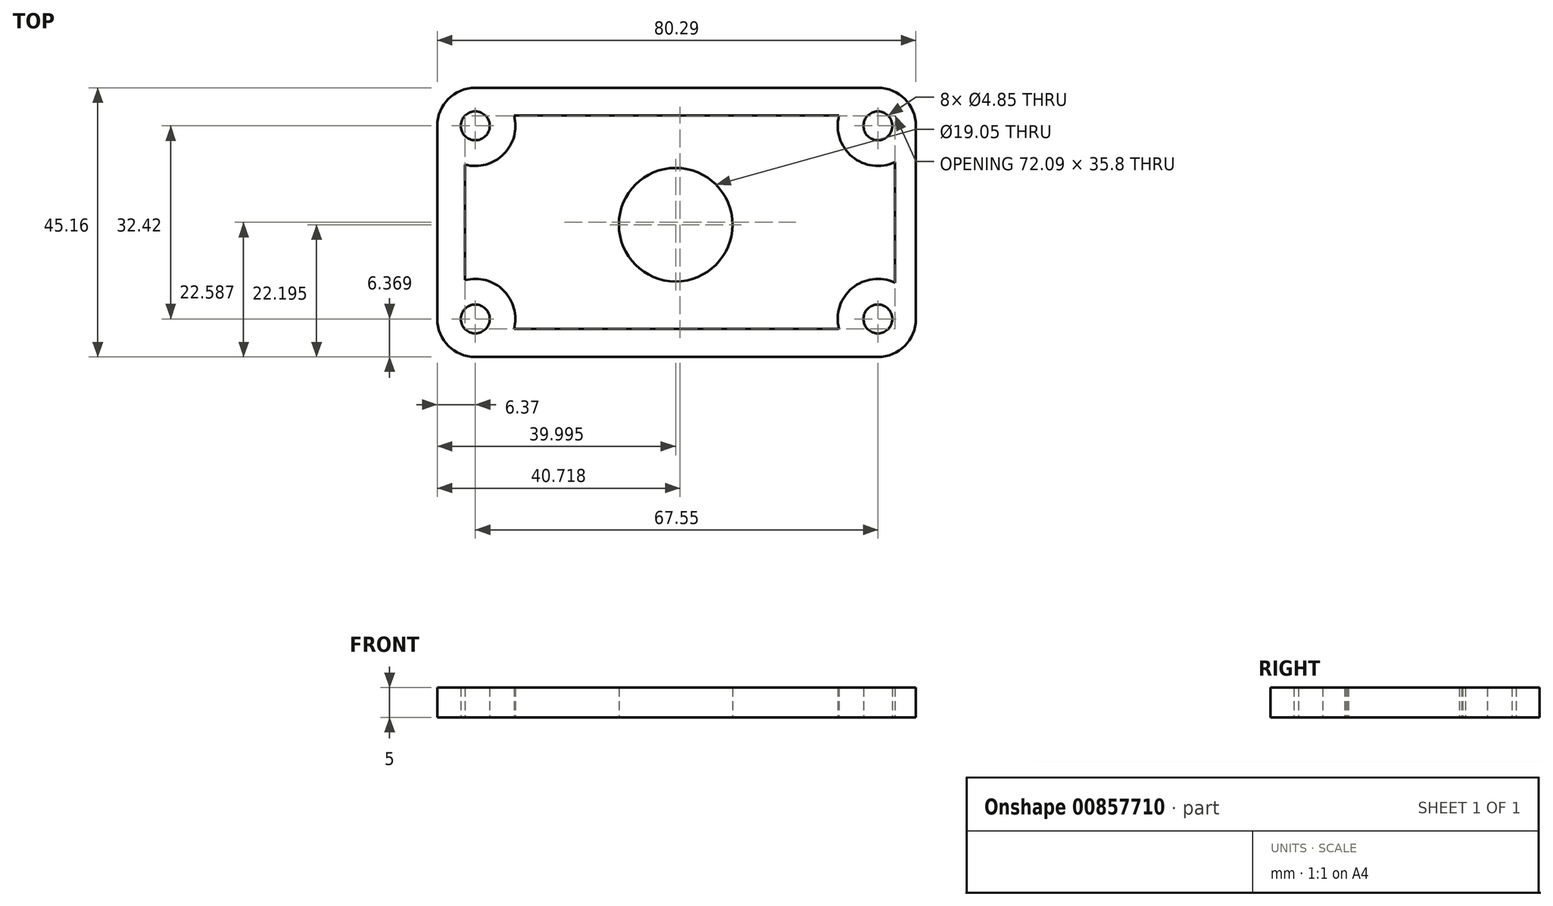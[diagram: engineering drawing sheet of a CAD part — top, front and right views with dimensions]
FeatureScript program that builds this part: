
annotation { "Feature Type Name" : "Feature", "Feature Type Description" : "" }
export const myFeature = defineFeature(function(context is Context, id is Id, definition is map)
    precondition{}
    {
        {
            var Q0;
            Q0=qCreatedBy(makeId("Top.planeOp"),FACE);
            var sketch = newSketch(context, id + "F0", { "sketchPlane" : qUnion([Q0])});
            skLineSegment(sketch, "E0.bottom", {"start": v(-49.8, 48.64) * mm, "end": v(17.74, 48.64) * mm});
            skLineSegment(sketch, "E0.top", {"start": v(-49.8, 3.48) * mm, "end": v(17.74, 3.48) * mm});
            skLineSegment(sketch, "E0.left", {"start": v(-56.18, 42.27) * mm, "end": v(-56.18, 9.85) * mm});
            skLineSegment(sketch, "E0.right", {"start": v(24.11, 42.27) * mm, "end": v(24.11, 9.85) * mm});
            skArc(sketch, "E1.filletArc", {"start": v(-49.8, 48.64) * mm, "mid": v(-54.32, 46.78) * mm, "end": v(-56.18, 42.27) * mm});
            skArc(sketch, "E2.filletArc", {"start": v(-56.18, 9.85) * mm, "mid": v(-54.32, 5.34) * mm, "end": v(-49.8, 3.48) * mm});
            skArc(sketch, "E3.filletArc", {"start": v(17.74, 3.48) * mm, "mid": v(22.25, 5.34) * mm, "end": v(24.11, 9.85) * mm});
            skArc(sketch, "E4.filletArc", {"start": v(24.11, 42.27) * mm, "mid": v(22.25, 46.78) * mm, "end": v(17.74, 48.64) * mm});
            skCircle(sketch, "E5", {"center": v(-49.8, 42.27) * mm, "radius": 2.42 * mm});
            skCircle(sketch, "E6", {"center": v(-49.8, 9.85) * mm, "radius": 2.42 * mm});
            skCircle(sketch, "E7", {"center": v(17.74, 9.85) * mm, "radius": 2.42 * mm});
            skCircle(sketch, "E8", {"center": v(17.74, 42.27) * mm, "radius": 2.42 * mm});
            skLineSegment(sketch, "E9", {"start": v(20.58, 36.16) * mm, "end": v(20.58, 16.17) * mm});
            skLineSegment(sketch, "E10", {"start": v(-43.29, 8.16) * mm, "end": v(11.22, 8.16) * mm});
            skLineSegment(sketch, "E11", {"start": v(-43.3, 43.97) * mm, "end": v(11.22, 43.97) * mm});
            skLineSegment(sketch, "E12", {"start": v(-51.5, 35.75) * mm, "end": v(-51.5, 16.17) * mm});
            skArc(sketch, "E13", {"start": v(-51.5, 35.75) * mm, "mid": v(-45.05, 37.5) * mm, "end": v(-43.3, 43.97) * mm});
            skArc(sketch, "E14", {"start": v(-43.29, 8.16) * mm, "mid": v(-45.05, 14.62) * mm, "end": v(-51.5, 16.37) * mm});
            skArc(sketch, "E15", {"start": v(20.58, 15.96) * mm, "mid": v(13.43, 15.03) * mm, "end": v(11.22, 8.16) * mm});
            skArc(sketch, "E16", {"start": v(11.22, 43.97) * mm, "mid": v(13.43, 37.1) * mm, "end": v(20.58, 36.16) * mm});
            skLineSegment(sketch, "E17", {"start": v(20.58, 16.17) * mm, "end": v(20.58, 15.96) * mm});
            skPoint(sketch, "E18.orphan", {"position": v(-43.9, 43.97) * mm});
            skPoint(sketch, "E19.orphan", {"position": v(-43.9, 8.16) * mm});
            skLineSegment(sketch, "E20", {"start": v(-49.96, 33.83) * mm, "end": v(-49.96, 18.5) * mm});
            skLineSegment(sketch, "E21", {"start": v(18.78, 18.5) * mm, "end": v(18.69, 33.83) * mm});
            skLineSegment(sketch, "E22", {"start": v(-41.59, 41.98) * mm, "end": v(8.14, 41.98) * mm});
            skLineSegment(sketch, "E23", {"start": v(-41.59, 9.85) * mm, "end": v(8.14, 9.85) * mm});
            skArc(sketch, "E24", {"start": v(-51.5, 33.66) * mm, "mid": v(-43.6, 36.06) * mm, "end": v(-41.2, 43.97) * mm});
            skArc(sketch, "E25", {"start": v(-41.2, 8.16) * mm, "mid": v(-43.6, 16.06) * mm, "end": v(-51.5, 18.46) * mm});
            skArc(sketch, "E26.trimOffspring", {"start": v(20.58, 18.15) * mm, "mid": v(11.97, 16.47) * mm, "end": v(9.13, 8.16) * mm});
            skArc(sketch, "E27.trimOffspring", {"start": v(9.13, 43.97) * mm, "mid": v(11.97, 35.66) * mm, "end": v(20.58, 33.97) * mm});
            skLineSegment(sketch, "E28", {"start": v(8.14, 9.85) * mm, "end": v(11, 9.85) * mm});
            skLineSegment(sketch, "E29", {"start": v(-41.59, 9.85) * mm, "end": v(-43.07, 9.85) * mm});
            skLineSegment(sketch, "E30", {"start": v(-49.96, 18.5) * mm, "end": v(-49.96, 16.58) * mm});
            skLineSegment(sketch, "E31", {"start": v(-41.59, 41.98) * mm, "end": v(-43.08, 41.98) * mm});
            skLineSegment(sketch, "E32", {"start": v(8.14, 41.98) * mm, "end": v(11.01, 41.98) * mm});
            skLineSegment(sketch, "E33", {"start": v(18.69, 33.83) * mm, "end": v(18.69, 35.6) * mm});
            skLineSegment(sketch, "E34", {"start": v(-49.96, 33.83) * mm, "end": v(-49.96, 35.53) * mm});
            skCircle(sketch, "E35", {"center": v(-16.18, 25.67) * mm, "radius": 14.98 * mm});
            skCircle(sketch, "E36", {"center": v(-16.18, 25.67) * mm, "radius": 13.1 * mm});
            skCircle(sketch, "E37", {"center": v(-16.18, 25.67) * mm, "radius": 9.53 * mm});
            skSolve(sketch);
        }
        {
            var Q0;
            Q0=makeQuery(id+"F0.imprint","IMPRINT",FACE,{"disambiguationData":[TD([[makeQuery(id+"F0.imprint","IMPRINT",EDGE,{"derivedFrom":sQuery(id+"F0.wireOp",EDGE,"E0.bottom")}),-1.0]])]});
            extrude(context, id + "F1", {"entities" : qUnion([Q0]), "depth" : 5 * mm, "offsetDistance" : 25 * mm});
        }
        {
            var Q0;
            Q0 = qSketchRegion(id + "F0", true);
            var Q1;
            {var subQ6=sQuery(id+"F0.wireOp",EDGE,"E29");Q1=makeQuery(id+"F0.imprint","IMPRINT",FACE,{"disambiguationData":[TD([[makeQuery(id+"F0.imprint","IMPRINT",EDGE,{"derivedFrom":subQ6}),-1.0]])]});}
            var Q2;
            {var subQ7=sQuery(id+"F0.wireOp",EDGE,"E29");Q2=makeQuery(id+"F0.imprint","IMPRINT",FACE,{"disambiguationData":[TD([[makeQuery(id+"F0.imprint","IMPRINT",EDGE,{"derivedFrom":subQ7}),1.0]])]});}
            var Q3;
            {var subQ7=sQuery(id+"F0.wireOp",EDGE,"E30");Q3=makeQuery(id+"F0.imprint","IMPRINT",FACE,{"disambiguationData":[TD([[makeQuery(id+"F0.imprint","IMPRINT",EDGE,{"derivedFrom":subQ7}),-1.0]])]});}
            var Q4;
            {var subQ0=sQuery(id+"F0.wireOp",EDGE,"E24");var subQ1=sQuery(id+"F0.wireOp",EDGE,"E12");var subQ2=makeQuery(id+"F0.imprint","INTERSECT",VERTEX,{"derivedFrom":[subQ1,subQ0]});Q4=makeQuery(id+"F0.imprint","IMPRINT",FACE,{"disambiguationData":[TD([[makeQuery(id+"F0.imprint","IMPRINT",EDGE,{"disambiguationData":[TD([[subQ2,-1.0]])],"derivedFrom":subQ1}),1.0]])]});}
            var Q5;
            {var subQ7=sQuery(id+"F0.wireOp",EDGE,"E34");Q5=makeQuery(id+"F0.imprint","IMPRINT",FACE,{"disambiguationData":[TD([[makeQuery(id+"F0.imprint","IMPRINT",EDGE,{"derivedFrom":subQ7}),1.0]])]});}
            var Q6;
            {var subQ5=sQuery(id+"F0.wireOp",EDGE,"E31");Q6=makeQuery(id+"F0.imprint","IMPRINT",FACE,{"disambiguationData":[TD([[makeQuery(id+"F0.imprint","IMPRINT",EDGE,{"derivedFrom":subQ5}),1.0]])]});}
            var Q7;
            {var subQ5=sQuery(id+"F0.wireOp",EDGE,"E31");Q7=makeQuery(id+"F0.imprint","IMPRINT",FACE,{"disambiguationData":[TD([[makeQuery(id+"F0.imprint","IMPRINT",EDGE,{"derivedFrom":subQ5}),-1.0]])]});}
            var Q8;
            {var subQ0=sQuery(id+"F0.wireOp",EDGE,"E24");var subQ1=sQuery(id+"F0.wireOp",EDGE,"E11");var subQ2=makeQuery(id+"F0.imprint","INTERSECT",VERTEX,{"derivedFrom":[subQ1,subQ0]});Q8=makeQuery(id+"F0.imprint","IMPRINT",FACE,{"disambiguationData":[TD([[makeQuery(id+"F0.imprint","IMPRINT",EDGE,{"disambiguationData":[TD([[subQ2,-1.0]])],"derivedFrom":subQ1}),-1.0]])]});}
            var Q9;
            {var subQ0=sQuery(id+"F0.wireOp",EDGE,"E16");var subQ1=sQuery(id+"F0.wireOp",EDGE,"E11");var subQ2=makeQuery(id+"F0.imprint","INTERSECT",VERTEX,{"derivedFrom":[subQ1,subQ0]});Q9=makeQuery(id+"F0.imprint","IMPRINT",FACE,{"disambiguationData":[TD([[makeQuery(id+"F0.imprint","IMPRINT",EDGE,{"disambiguationData":[TD([[subQ2,1.0]])],"derivedFrom":subQ1}),-1.0]])]});}
            var Q10;
            {var subQ7=sQuery(id+"F0.wireOp",EDGE,"E33");Q10=makeQuery(id+"F0.imprint","IMPRINT",FACE,{"disambiguationData":[TD([[makeQuery(id+"F0.imprint","IMPRINT",EDGE,{"derivedFrom":subQ7}),1.0]])]});}
            var Q11;
            {var subQ7=sQuery(id+"F0.wireOp",EDGE,"E33");Q11=makeQuery(id+"F0.imprint","IMPRINT",FACE,{"disambiguationData":[TD([[makeQuery(id+"F0.imprint","IMPRINT",EDGE,{"derivedFrom":subQ7}),-1.0]])]});}
            var Q12;
            {var subQ0=sQuery(id+"F0.wireOp",EDGE,"E26.trimOffspring");var subQ1=sQuery(id+"F0.wireOp",EDGE,"E9");var subQ2=makeQuery(id+"F0.imprint","INTERSECT",VERTEX,{"derivedFrom":[subQ1,subQ0]});Q12=makeQuery(id+"F0.imprint","IMPRINT",FACE,{"disambiguationData":[TD([[makeQuery(id+"F0.imprint","IMPRINT",EDGE,{"disambiguationData":[TD([[subQ2,1.0]])],"derivedFrom":subQ1}),-1.0]])]});}
            var Q13;
            {var subQ4=sQuery(id+"F0.wireOp",EDGE,"E17");Q13=makeQuery(id+"F0.imprint","IMPRINT",FACE,{"disambiguationData":[TD([[makeQuery(id+"F0.imprint","IMPRINT",EDGE,{"derivedFrom":subQ4}),-1.0]])]});}
            var Q14;
            {var subQ0=sQuery(id+"F0.wireOp",EDGE,"E15");var subQ1=sQuery(id+"F0.wireOp",EDGE,"E10");var subQ2=makeQuery(id+"F0.imprint","INTERSECT",VERTEX,{"derivedFrom":[subQ1,subQ0]});Q14=makeQuery(id+"F0.imprint","IMPRINT",FACE,{"disambiguationData":[TD([[makeQuery(id+"F0.imprint","IMPRINT",EDGE,{"disambiguationData":[TD([[subQ2,1.0]])],"derivedFrom":subQ1}),1.0]])]});}
            var Q15;
            {var subQ1=sQuery(id+"F0.wireOp",EDGE,"E10");var subQ5=sQuery(id+"F0.wireOp",EDGE,"E25");var subQ6=makeQuery(id+"F0.imprint","INTERSECT",VERTEX,{"derivedFrom":[subQ1,subQ5]});Q15=makeQuery(id+"F0.imprint","IMPRINT",FACE,{"disambiguationData":[TD([[makeQuery(id+"F0.imprint","IMPRINT",EDGE,{"disambiguationData":[TD([[subQ6,-1.0]])],"derivedFrom":subQ1}),1.0]])]});}
            var Q16;
            Q16=makeQuery(id+"F0.imprint","IMPRINT",FACE,{"disambiguationData":[TD([[makeQuery(id+"F0.imprint","IMPRINT",EDGE,{"derivedFrom":sQuery(id+"F0.wireOp",EDGE,"E35")}),-1.0]])]});
            var Q17;
            Q17=makeQuery(id+"F0.imprint","IMPRINT",FACE,{"disambiguationData":[TD([[makeQuery(id+"F0.imprint","IMPRINT",EDGE,{"derivedFrom":sQuery(id+"F0.wireOp",EDGE,"E36")}),1.0]])]});
            var Q18;
            Q18=makeQuery(id+"F0.imprint","IMPRINT",FACE,{"disambiguationData":[TD([[makeQuery(id+"F0.imprint","IMPRINT",EDGE,{"derivedFrom":sQuery(id+"F0.wireOp",EDGE,"E35")}),1.0]])]});
            extrude(context, id + "F2", {"entities" : qUnion([Q0, Q1, Q2, Q3, Q4, Q5, Q6, Q7, Q8, Q9, Q10, Q11, Q12, Q13, Q14, Q15, Q16, Q17, Q18]), "depth" : 5 * mm, "offsetDistance" : 25 * mm});
        }
    });
